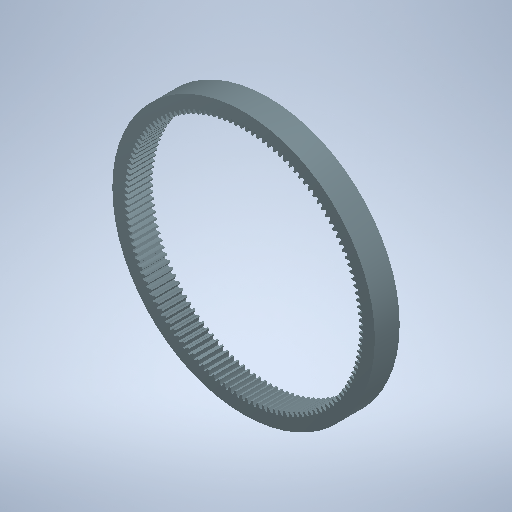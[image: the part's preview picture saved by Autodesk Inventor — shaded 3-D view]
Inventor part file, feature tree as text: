
AUTODESK INVENTOR PART (.ipt)
format: ipt  version: 2025 (Build 290162010, 162A)  size: 774,656 bytes
history: native  units: mm (DEFAULTED — no unit token found)
features: plane x3, other x3, sketch x2, extrude x1
ambient origin geometry x8: Origin, YZ Plane, XZ Plane, XY Plane, X Axis, Y Axis, Z Axis, Center Point
bodies: Body1 (feature_tree), Body2 (feature_tree)
feature tree (9):
  extrude  "Extrusion1"  Depth=7.0mm TaperAngle=0.0deg
  plane  "Work Plane2"
  plane  "Work Plane8"
  plane  "Work Plane9"
  other  "Stirnzahnrad"
  sketch  "Skizze3"  dims[d3=66.0mm d4=10.0mm d5=0.0mm d16=24.75mm d17=0.0mm d34=0.237999mm d39=0.0mm d45=0.0mm d47=24.75mm d50=0.0mm d51=0.0mm d52=24.75mm d53=66.0mm]
  sketch  "Sketch1"  dims[d0=73.975mm d1=7.0mm d2=0.0mm]
  other  "Srf1"
  other  "Flankendurchmesser"
